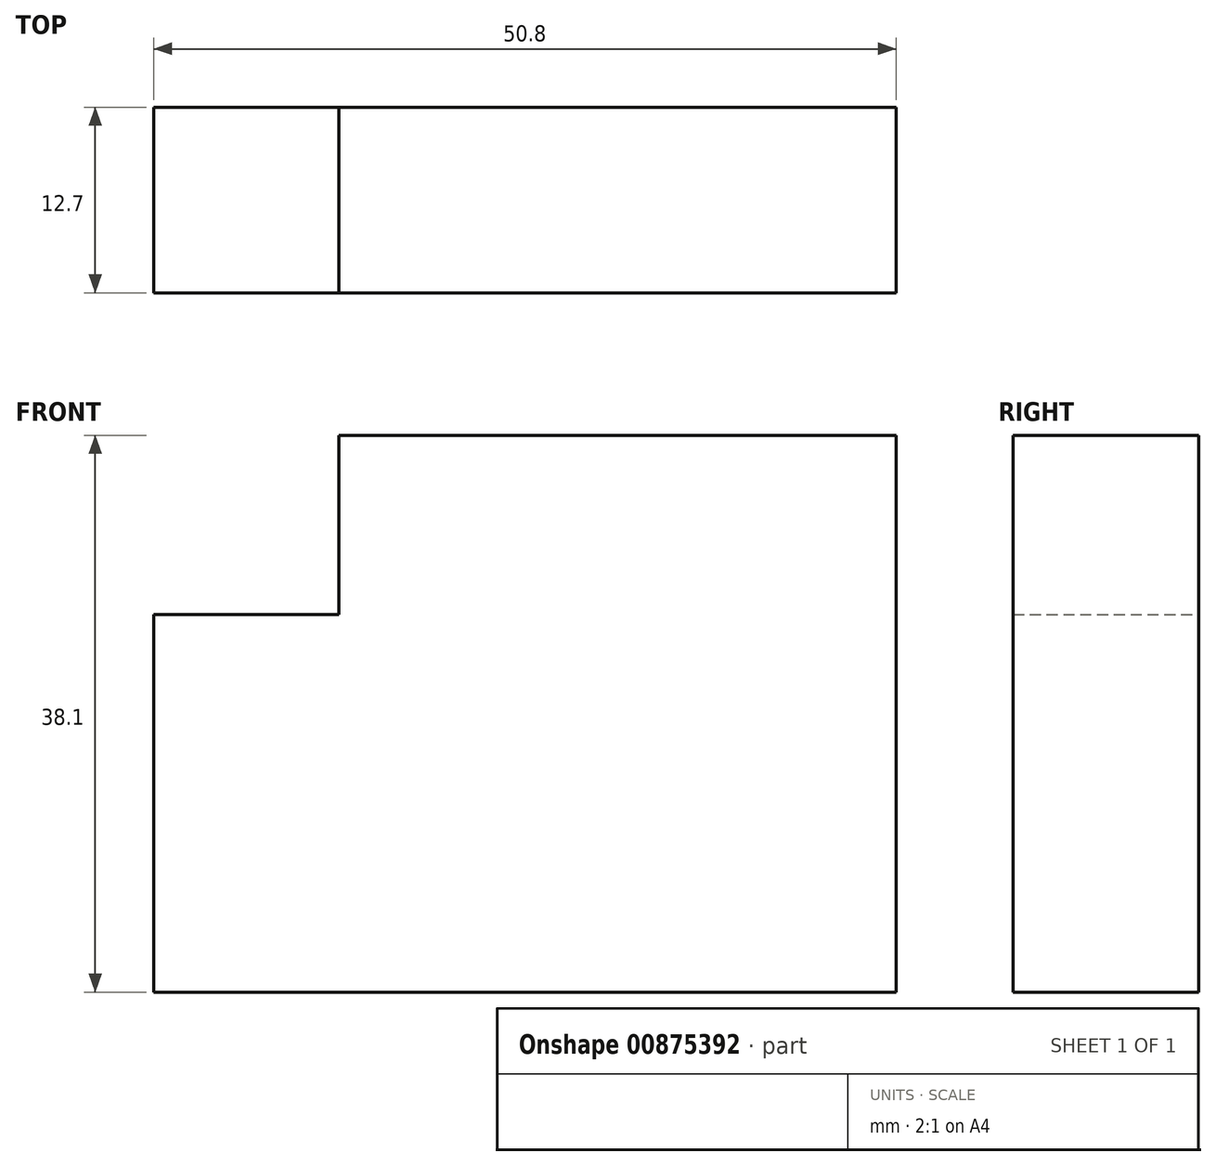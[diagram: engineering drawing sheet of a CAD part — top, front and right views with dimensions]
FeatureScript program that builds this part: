
annotation { "Feature Type Name" : "Feature", "Feature Type Description" : "" }
export const myFeature = defineFeature(function(context is Context, id is Id, definition is map)
    precondition{}
    {
        {
            var Q0;
            Q0=qCreatedBy(makeId("Front.planeOp"),FACE);
            var sketch = newSketch(context, id + "F0", { "sketchPlane" : qUnion([Q0])});
            skLineSegment(sketch, "E0.bottom", {"start": v(-26.83, 21.13) * mm, "end": v(23.97, 21.13) * mm});
            skLineSegment(sketch, "E0.top", {"start": v(-26.83, -16.97) * mm, "end": v(23.97, -16.97) * mm});
            skLineSegment(sketch, "E0.left", {"start": v(-26.83, 21.13) * mm, "end": v(-26.83, -16.97) * mm});
            skLineSegment(sketch, "E0.right", {"start": v(23.97, 21.13) * mm, "end": v(23.97, -16.97) * mm});
            skSolve(sketch);
        }
        {
            var Q0;
            Q0=makeQuery(id+"F0.imprint","IMPRINT",FACE,{"disambiguationData":[TD([[makeQuery(id+"F0.imprint","IMPRINT",EDGE,{"derivedFrom":sQuery(id+"F0.wireOp",EDGE,"E0.bottom")}),-1.0]])]});
            var sketch = newSketch(context, id + "F1", { "sketchPlane" : qUnion([Q0])});
            skLineSegment(sketch, "E1.bottom", {"start": v(-26.85, 21.56) * mm, "end": v(-14.15, 21.56) * mm});
            skLineSegment(sketch, "E1.top", {"start": v(-26.85, 8.86) * mm, "end": v(-14.15, 8.86) * mm});
            skLineSegment(sketch, "E1.left", {"start": v(-26.85, 21.56) * mm, "end": v(-26.85, 8.86) * mm});
            skLineSegment(sketch, "E1.right", {"start": v(-14.15, 21.56) * mm, "end": v(-14.15, 8.86) * mm});
            skSolve(sketch);
        }
        {
            var Q0;
            {var subQ0=sQuery(id+"F1.wireOp",EDGE,"E1.right");Q0=makeQuery(id+"F1.imprint","IMPRINT",FACE,{"disambiguationData":[TD([[makeQuery(id+"F1.imprint","IMPRINT",EDGE,{"derivedFrom":subQ0}),1.0]])]});}
            extrude(context, id + "F2", {"entities" : qUnion([Q0]), "depth" : 12.7 * mm, "offsetDistance" : 25.4 * mm});
        }
    });
